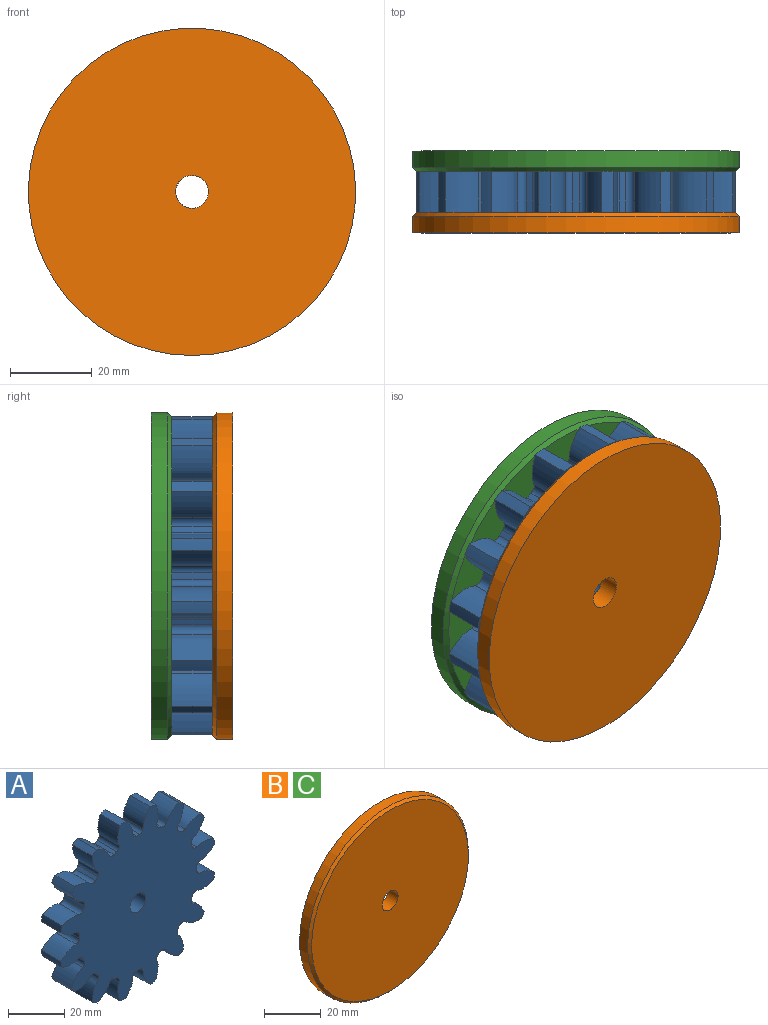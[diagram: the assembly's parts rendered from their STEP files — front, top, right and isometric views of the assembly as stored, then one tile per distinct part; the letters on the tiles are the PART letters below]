
ASSEMBLY  parts=3 mates=2
PART A: 99 faces, bbox 77.9x10x77.9 mm
  f0: cylinder r=39.38mm len=10mm, axis (0,1,0), area 29.1mm2, adj f15,f18,f89,f96
  f1: cylinder r=39.38mm len=10mm, axis (0,1,0), area 29.1mm2, adj f15,f18,f64,f91
  f2: cylinder r=39.38mm len=10mm, axis (0,1,0), area 29.1mm2, adj f15,f18,f86,f94
  f3: cylinder r=39.38mm len=10mm, axis (0,1,0), area 29.1mm2, adj f15,f18,f74,f81
  f4: cylinder r=39.38mm len=10mm, axis (0,1,0), area 29.1mm2, adj f15,f18,f44,f76
  f5: cylinder r=39.38mm len=10mm, axis (0,1,0), area 29.1mm2, adj f15,f18,f71,f79
  f6: cylinder r=39.38mm len=10mm, axis (0,1,0), area 29.1mm2, adj f15,f18,f66,f69
  f7: cylinder r=39.38mm len=10mm, axis (0,1,0), area 29.1mm2, adj f15,f18,f54,f61
  f8: cylinder r=39.38mm len=10mm, axis (0,1,0), area 29.1mm2, adj f15,f18,f24,f56
  f9: cylinder r=39.38mm len=10mm, axis (0,1,0), area 29.1mm2, adj f15,f18,f51,f59
  f10: cylinder r=39.38mm len=10mm, axis (0,1,0), area 29.1mm2, adj f15,f18,f46,f49
  f11: cylinder r=39.38mm len=10mm, axis (0,1,0), area 29.1mm2, adj f15,f18,f34,f41
  f12: cylinder r=39.38mm len=10mm, axis (0,1,0), area 29.1mm2, adj f15,f18,f19,f36
  f13: cylinder r=39.38mm len=10mm, axis (0,1,0), area 29.1mm2, adj f15,f18,f31,f39
  f14: cylinder r=39.38mm len=10mm, axis (0,1,0), area 29.1mm2, adj f15,f18,f26,f29
  f15: plane 77.85x77.85mm, normal (0,-1,0), area 3694.9mm2, adj f0,f1,f2,f3,f4,f5,f6,f7
  f16: cylinder r=4mm len=10mm, axis (0,1,0), area 251.3mm2, adj f15,f18
  f17: cylinder r=39.38mm len=10mm, axis (0,1,0), area 29.1mm2, adj f15,f18,f21,f84
  f18: plane 77.85x77.85mm, normal (0,1,0), area 3694.9mm2, adj f0,f1,f2,f3,f4,f5,f6,f7
  f19: extruded ~10x7.72mm, area 87.7mm2, adj f12,f15,f18,f22
  f20: cylinder r=29.53mm len=10mm, axis (0,1,0), area 15.5mm2, adj f15,f18,f22,f23
  f21: extruded ~10x7.72mm, area 87.7mm2, adj f15,f17,f18,f23
  f22: cylinder r=1.78mm len=10mm, axis (0,1,0), area 27mm2, adj f15,f18,f19,f20
  f23: cylinder r=1.78mm len=10mm, axis (0,1,0), area 27mm2, adj f15,f18,f20,f21
  f24: extruded ~10x7.72mm, area 87.7mm2, adj f8,f15,f18,f27
  f25: cylinder r=29.53mm len=10mm, axis (0,1,0), area 15.5mm2, adj f15,f18,f27,f28
  f26: extruded ~10x7.72mm, area 87.7mm2, adj f14,f15,f18,f28
  f27: cylinder r=1.78mm len=10mm, axis (0,1,0), area 27mm2, adj f15,f18,f24,f25
  f28: cylinder r=1.78mm len=10mm, axis (0,1,0), area 27mm2, adj f15,f18,f25,f26
  f29: extruded ~10x8.53mm, area 87.7mm2, adj f14,f15,f18,f32
  f30: cylinder r=29.53mm len=10mm, axis (0,1,0), area 15.5mm2, adj f15,f18,f32,f33
  f31: extruded ~10x6.33mm, area 87.7mm2, adj f13,f15,f18,f33
  f32: cylinder r=1.78mm len=10mm, axis (0,1,0), area 27mm2, adj f15,f18,f29,f30
  f33: cylinder r=1.78mm len=10mm, axis (0,1,0), area 27mm2, adj f15,f18,f30,f31
  f34: extruded ~10x6.33mm, area 87.7mm2, adj f11,f15,f18,f37
  f35: cylinder r=29.53mm len=10mm, axis (0,1,0), area 15.5mm2, adj f15,f18,f37,f38
  f36: extruded ~10x8.53mm, area 87.7mm2, adj f12,f15,f18,f38
  f37: cylinder r=1.78mm len=10mm, axis (0,1,0), area 27mm2, adj f15,f18,f34,f35
  f38: cylinder r=1.78mm len=10mm, axis (0,1,0), area 27mm2, adj f15,f18,f35,f36
  f39: extruded ~10x8.04mm, area 87.7mm2, adj f13,f15,f18,f42
  f40: cylinder r=29.53mm len=10mm, axis (0,1,0), area 15.5mm2, adj f15,f18,f42,f43
  f41: extruded ~10x8.04mm, area 87.7mm2, adj f11,f15,f18,f43
  f42: cylinder r=1.78mm len=10mm, axis (0,1,0), area 27mm2, adj f15,f18,f39,f40
  f43: cylinder r=1.78mm len=10mm, axis (0,1,0), area 27mm2, adj f15,f18,f40,f41
  f44: extruded ~10x7.72mm, area 87.7mm2, adj f4,f15,f18,f47
  f45: cylinder r=29.53mm len=10mm, axis (0,1,0), area 15.5mm2, adj f15,f18,f47,f48
  f46: extruded ~10x7.72mm, area 87.7mm2, adj f10,f15,f18,f48
  f47: cylinder r=1.78mm len=10mm, axis (0,1,0), area 27mm2, adj f15,f18,f44,f45
  f48: cylinder r=1.78mm len=10mm, axis (0,1,0), area 27mm2, adj f15,f18,f45,f46
  f49: extruded ~10x8.53mm, area 87.7mm2, adj f10,f15,f18,f52
  f50: cylinder r=29.53mm len=10mm, axis (0,1,0), area 15.5mm2, adj f15,f18,f52,f53
  f51: extruded ~10x6.33mm, area 87.7mm2, adj f9,f15,f18,f53
  f52: cylinder r=1.78mm len=10mm, axis (0,1,0), area 27mm2, adj f15,f18,f49,f50
  f53: cylinder r=1.78mm len=10mm, axis (0,1,0), area 27mm2, adj f15,f18,f50,f51
  f54: extruded ~10x6.33mm, area 87.7mm2, adj f7,f15,f18,f57
  f55: cylinder r=29.53mm len=10mm, axis (0,1,0), area 15.5mm2, adj f15,f18,f57,f58
  f56: extruded ~10x8.53mm, area 87.7mm2, adj f8,f15,f18,f58
  f57: cylinder r=1.78mm len=10mm, axis (0,1,0), area 27mm2, adj f15,f18,f54,f55
  f58: cylinder r=1.78mm len=10mm, axis (0,1,0), area 27mm2, adj f15,f18,f55,f56
  f59: extruded ~10x8.04mm, area 87.7mm2, adj f9,f15,f18,f62
  f60: cylinder r=29.53mm len=10mm, axis (0,1,0), area 15.5mm2, adj f15,f18,f62,f63
  f61: extruded ~10x8.04mm, area 87.7mm2, adj f7,f15,f18,f63
  f62: cylinder r=1.78mm len=10mm, axis (0,1,0), area 27mm2, adj f15,f18,f59,f60
  f63: cylinder r=1.78mm len=10mm, axis (0,1,0), area 27mm2, adj f15,f18,f60,f61
  f64: extruded ~10x7.72mm, area 87.7mm2, adj f1,f15,f18,f67
  f65: cylinder r=29.53mm len=10mm, axis (0,1,0), area 15.5mm2, adj f15,f18,f67,f68
  f66: extruded ~10x7.72mm, area 87.7mm2, adj f6,f15,f18,f68
  f67: cylinder r=1.78mm len=10mm, axis (0,1,0), area 27mm2, adj f15,f18,f64,f65
  f68: cylinder r=1.78mm len=10mm, axis (0,1,0), area 27mm2, adj f15,f18,f65,f66
  f69: extruded ~10x8.53mm, area 87.7mm2, adj f6,f15,f18,f72
  f70: cylinder r=29.53mm len=10mm, axis (0,1,0), area 15.5mm2, adj f15,f18,f72,f73
  f71: extruded ~10x6.33mm, area 87.7mm2, adj f5,f15,f18,f73
  f72: cylinder r=1.78mm len=10mm, axis (0,1,0), area 27mm2, adj f15,f18,f69,f70
  f73: cylinder r=1.78mm len=10mm, axis (0,1,0), area 27mm2, adj f15,f18,f70,f71
  f74: extruded ~10x6.33mm, area 87.7mm2, adj f3,f15,f18,f77
  f75: cylinder r=29.53mm len=10mm, axis (0,1,0), area 15.5mm2, adj f15,f18,f77,f78
  f76: extruded ~10x8.53mm, area 87.7mm2, adj f4,f15,f18,f78
  f77: cylinder r=1.78mm len=10mm, axis (0,1,0), area 27mm2, adj f15,f18,f74,f75
  f78: cylinder r=1.78mm len=10mm, axis (0,1,0), area 27mm2, adj f15,f18,f75,f76
  f79: extruded ~10x8.04mm, area 87.7mm2, adj f5,f15,f18,f82
  f80: cylinder r=29.53mm len=10mm, axis (0,1,0), area 15.5mm2, adj f15,f18,f82,f83
  f81: extruded ~10x8.04mm, area 87.7mm2, adj f3,f15,f18,f83
  f82: cylinder r=1.78mm len=10mm, axis (0,1,0), area 27mm2, adj f15,f18,f79,f80
  f83: cylinder r=1.78mm len=10mm, axis (0,1,0), area 27mm2, adj f15,f18,f80,f81
  f84: extruded ~10x8.53mm, area 87.7mm2, adj f15,f17,f18,f87
  f85: cylinder r=29.53mm len=10mm, axis (0,1,0), area 15.5mm2, adj f15,f18,f87,f88
  f86: extruded ~10x6.33mm, area 87.7mm2, adj f2,f15,f18,f88
  f87: cylinder r=1.78mm len=10mm, axis (0,1,0), area 27mm2, adj f15,f18,f84,f85
  f88: cylinder r=1.78mm len=10mm, axis (0,1,0), area 27mm2, adj f15,f18,f85,f86
  f89: extruded ~10x6.33mm, area 87.7mm2, adj f0,f15,f18,f92
  f90: cylinder r=29.53mm len=10mm, axis (0,1,0), area 15.5mm2, adj f15,f18,f92,f93
  f91: extruded ~10x8.53mm, area 87.7mm2, adj f1,f15,f18,f93
  f92: cylinder r=1.78mm len=10mm, axis (0,1,0), area 27mm2, adj f15,f18,f89,f90
  f93: cylinder r=1.78mm len=10mm, axis (0,1,0), area 27mm2, adj f15,f18,f90,f91
  f94: extruded ~10x8.04mm, area 87.7mm2, adj f2,f15,f18,f97
  f95: cylinder r=29.53mm len=10mm, axis (0,1,0), area 15.5mm2, adj f15,f18,f97,f98
  f96: extruded ~10x8.04mm, area 87.7mm2, adj f0,f15,f18,f98
  f97: cylinder r=1.78mm len=10mm, axis (0,1,0), area 27mm2, adj f15,f18,f94,f95
  f98: cylinder r=1.78mm len=10mm, axis (0,1,0), area 27mm2, adj f15,f18,f95,f96
PART B: 5 faces, bbox 80x5x80 mm
  f0: cylinder r=4mm len=8mm, axis (0,1,0), area 125.7mm2, adj f2,f3
  f1: cylinder r=40mm len=80mm, axis (0,1,0), area 1005.3mm2, adj f3,f4
  f2: plane 78x78mm, normal (0,-1,0), area 4728.1mm2, adj f0,f4
  f3: plane 80x80mm, normal (0,1,0), area 4976.3mm2, adj f0,f1
  f4: cone r=39mm half-angle=45deg, axis (0,1,0), area 351mm2, adj f1,f2
PART C: same geometry as B
PLACE A rot(axis=(1,0,0),0deg) t=(0,-5,0)mm
PLACE B rot(axis=(0,0,1),180deg) t=(0,-20,0)mm
PLACE C at identity
MATE fastened A.f0 <-> C.f0  axis (0,1,0) through (0,-5,0)mm
MATE fastened A.f0 <-> B.f0  axis (0,-1,0) through (0,-15,0)mm
